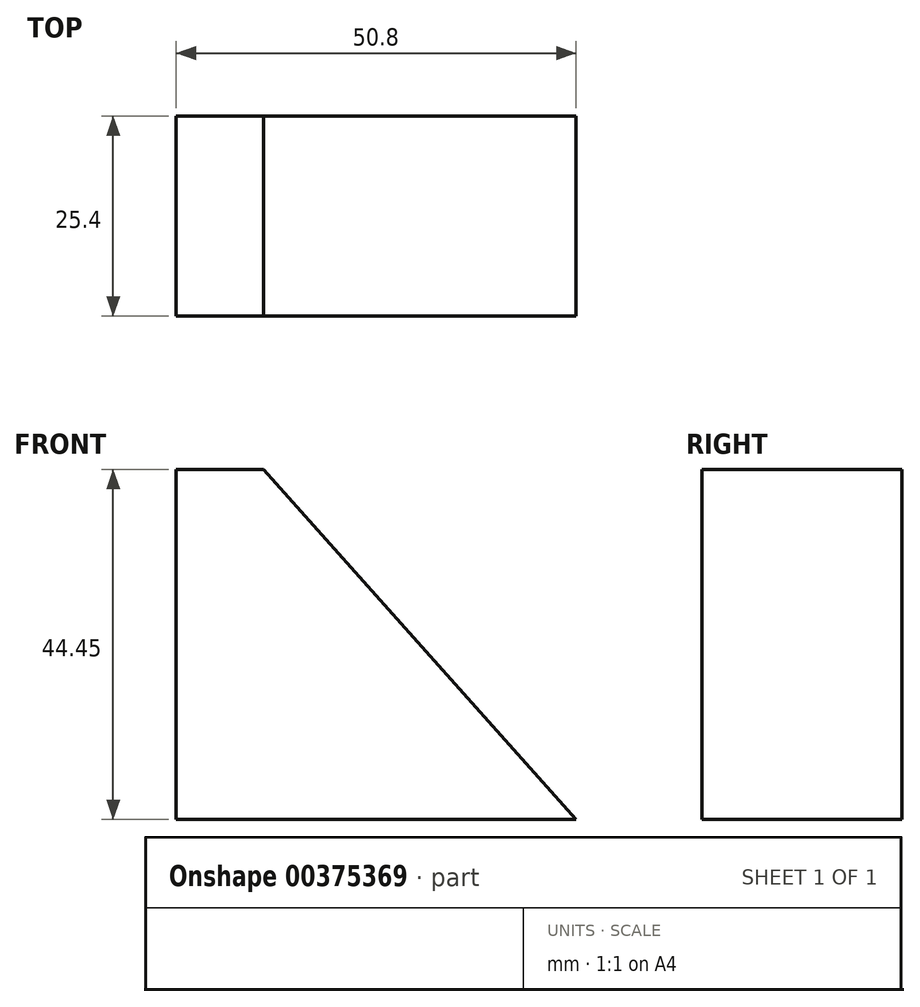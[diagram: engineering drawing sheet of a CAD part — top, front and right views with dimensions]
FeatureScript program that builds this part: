
annotation { "Feature Type Name" : "Feature", "Feature Type Description" : "" }
export const myFeature = defineFeature(function(context is Context, id is Id, definition is map)
    precondition{}
    {
        {
            var Q0;
            Q0=qCreatedBy(makeId("Front.planeOp"),FACE);
            var sketch = newSketch(context, id + "F0", { "sketchPlane" : qUnion([Q0])});
            skLineSegment(sketch, "E0", {"start": v(0, 0) * mm, "end": v(0, 44.45) * mm});
            skLineSegment(sketch, "E1", {"start": v(0, 44.45) * mm, "end": v(11.1, 44.45) * mm});
            skLineSegment(sketch, "E2", {"start": v(11.1, 44.45) * mm, "end": v(50.8, 0) * mm});
            skLineSegment(sketch, "E3", {"start": v(0, 0) * mm, "end": v(50.8, 0) * mm});
            skSolve(sketch);
        }
        {
            var Q0;
            Q0 = qSketchRegion(id + "F0", true);
            extrude(context, id + "F1", {"entities" : qUnion([Q0]), "depth" : 25.4 * mm});
        }
    });
